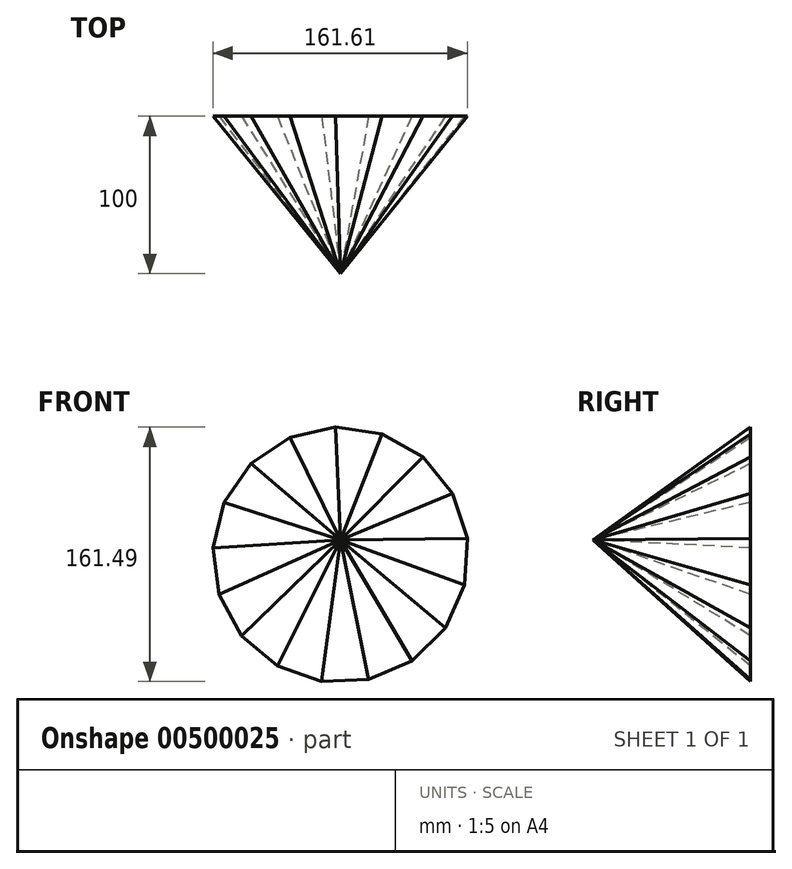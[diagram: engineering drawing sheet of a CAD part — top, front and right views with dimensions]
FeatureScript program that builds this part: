
annotation { "Feature Type Name" : "Feature", "Feature Type Description" : "" }
export const myFeature = defineFeature(function(context is Context, id is Id, definition is map)
    precondition{}
    {
        {
            var Q0;
            Q0=qCreatedBy(makeId("Front.planeOp"),FACE);
            var sketch = newSketch(context, id + "F0", { "sketchPlane" : qUnion([Q0])});
            skCircle(sketch, "E0.cCircle", {"center": v(0, 0) * mm, "radius": 81.21 * mm, "construction": true});
            skLineSegment(sketch, "E0.0", {"start": v(-74.02, 33.42) * mm, "end": v(-56.94, 57.9) * mm});
            skLineSegment(sketch, "E0.1", {"start": v(-56.94, 57.9) * mm, "end": v(-32.18, 74.56) * mm});
            skLineSegment(sketch, "E0.2", {"start": v(-32.18, 74.56) * mm, "end": v(-3.07, 81.15) * mm});
            skLineSegment(sketch, "E0.3", {"start": v(-3.07, 81.15) * mm, "end": v(26.45, 76.78) * mm});
            skLineSegment(sketch, "E0.4", {"start": v(26.45, 76.78) * mm, "end": v(52.4, 62.04) * mm});
            skLineSegment(sketch, "E0.5", {"start": v(52.4, 62.04) * mm, "end": v(71.28, 38.93) * mm});
            skLineSegment(sketch, "E0.6", {"start": v(71.28, 38.93) * mm, "end": v(80.52, 10.55) * mm});
            skLineSegment(sketch, "E0.7", {"start": v(80.52, 10.55) * mm, "end": v(78.9, -19.25) * mm});
            skLineSegment(sketch, "E0.8", {"start": v(78.9, -19.25) * mm, "end": v(66.61, -46.45) * mm});
            skLineSegment(sketch, "E0.9", {"start": v(66.61, -46.45) * mm, "end": v(45.34, -67.38) * mm});
            skLineSegment(sketch, "E0.10", {"start": v(45.34, -67.38) * mm, "end": v(17.93, -79.2) * mm});
            skLineSegment(sketch, "E0.11", {"start": v(17.93, -79.2) * mm, "end": v(-11.9, -80.34) * mm});
            skLineSegment(sketch, "E0.12", {"start": v(-11.9, -80.34) * mm, "end": v(-40.1, -70.62) * mm});
            skLineSegment(sketch, "E0.13", {"start": v(-40.1, -70.62) * mm, "end": v(-62.91, -51.36) * mm});
            skLineSegment(sketch, "E0.14", {"start": v(-62.91, -51.36) * mm, "end": v(-77.22, -25.17) * mm});
            skLineSegment(sketch, "E0.15", {"start": v(-77.22, -25.17) * mm, "end": v(-81.1, 4.43) * mm});
            skLineSegment(sketch, "E0.16", {"start": v(-81.1, 4.43) * mm, "end": v(-74.02, 33.42) * mm});
            skSolve(sketch);
        }
        {
            var Q0;
            Q0=makeQuery(id+"F0.imprint","IMPRINT",FACE,{"disambiguationData":[TD([[makeQuery(id+"F0.imprint","IMPRINT",EDGE,{"derivedFrom":sQuery(id+"F0.wireOp",EDGE,"E0.0")}),-1.0]])]});
            cPlane(context, id + "F1", {"entities" : qUnion([Q0]), "cplaneType" : CPlaneType.OFFSET, "offset" : 100 * mm, "width" : 150 * mm, "height" : 150 * mm});
        }
        {
            var Q0;
            Q0=qCreatedBy(id+"F1.planeOp",FACE);
            var sketch = newSketch(context, id + "F2", { "sketchPlane" : qUnion([Q0])});
            skPoint(sketch, "E1", {"position": v(0, 9.44) * mm});
            skSolve(sketch);
        }
        {
            var Q0;
            Q0=makeQuery(id+"F0.imprint","IMPRINT",FACE,{"disambiguationData":[TD([[makeQuery(id+"F0.imprint","IMPRINT",EDGE,{"derivedFrom":sQuery(id+"F0.wireOp",EDGE,"E0.0")}),-1.0]])]});
            var Q1;
            Q1=sQuery(id+"F2.wireOp",VERTEX,"E1");
            loft(context, id + "F3", {"sheetProfilesArray" : [{ "sheetProfileEntities" : qUnion([Q0]) }, { "sheetProfileEntities" : qUnion([Q1]) }]});
        }
    });
